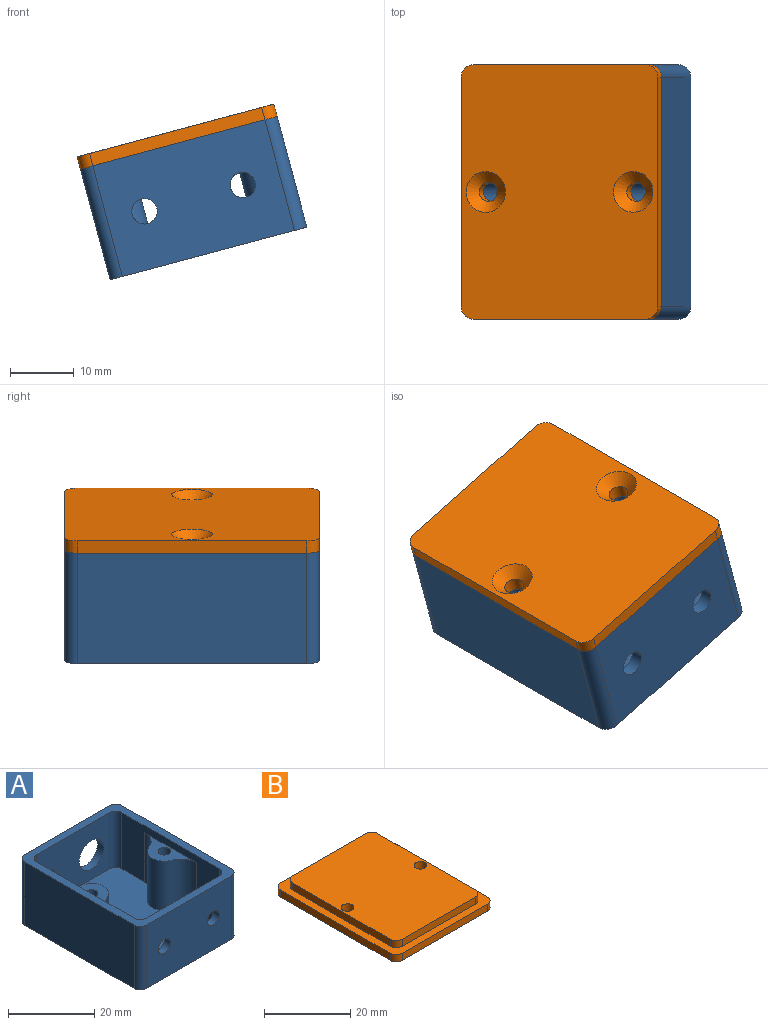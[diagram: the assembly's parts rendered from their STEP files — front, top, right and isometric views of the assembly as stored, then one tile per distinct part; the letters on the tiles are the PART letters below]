
ASSEMBLY  parts=2 mates=1
PART A: 35 faces, bbox 32x40x18 mm
  f0: plane 36x28mm, normal (0,0,1), area 907.9mm2, adj f1,f2,f9,f10,f15,f17,f23,f24
  f1: plane 32x16mm, normal (-1,0,0), area 274.4mm2, adj f0,f7,f18,f23,f24,f27,f30
  f2: plane 32x16mm, normal (1,0,0), area 274.4mm2, adj f0,f7,f16,f25,f26,f28,f29
  f3: plane 28x18mm, normal (0,-1,0), area 478.9mm2, adj f7,f8,f13,f14,f31,f34
  f4: plane 36x18mm, normal (1,0,0), area 648mm2, adj f7,f8,f31,f32
  f5: plane 28x18mm, normal (0,1,0), area 434.1mm2, adj f7,f8,f11,f12,f32,f33
  f6: plane 36x18mm, normal (-1,0,0), area 648mm2, adj f7,f8,f33,f34
  f7: plane 40x32mm, normal (0,0,1), area 272mm2, adj f1,f2,f3,f4,f5,f6,f9,f10
  f8: plane 40x32mm, normal (0,0,-1), area 1276.6mm2, adj f3,f4,f5,f6,f31,f32,f33,f34
  f9: plane 24x16mm, normal (0,-1,0), area 314.1mm2, adj f0,f7,f11,f12,f27,f28
  f10: plane 24x16mm, normal (0,1,0), area 358.9mm2, adj f0,f7,f13,f14,f29,f30
  f11: cylinder r=2.5mm len=5mm, axis (0,1,0), area 31.4mm2, adj f5,f9
  f12: cylinder r=4mm len=8mm, axis (0,1,0), area 50.3mm2, adj f5,f9
  f13: cylinder r=2mm len=4mm, axis (0,-1,0), area 25.1mm2, adj f3,f10
  f14: cylinder r=2mm len=4mm, axis (0,-1,0), area 25.1mm2, adj f3,f10
  f15: cylinder r=4mm len=14mm, axis (0,0,-1), area 137.9mm2, adj f0,f16,f25,f26
  f16: plane 16.97x6mm, normal (0,0,1), area 41.2mm2, adj f2,f15,f21,f25,f26
  f17: cylinder r=4mm len=14mm, axis (0,0,-1), area 137.9mm2, adj f0,f18,f23,f24
  f18: plane 16.97x6mm, normal (0,0,1), area 41.2mm2, adj f1,f17,f19,f23,f24
  f19: cylinder r=1.5mm len=8mm, axis (0,0,1), area 75.4mm2, adj f18,f20
  f20: plane 3x3mm, normal (0,0,1), area 7.1mm2, adj f19
  f21: cylinder r=1.5mm len=8mm, axis (0,0,1), area 75.4mm2, adj f16,f22
  f22: plane 3x3mm, normal (0,0,1), area 7.1mm2, adj f21
  f23: cylinder r=5mm len=14mm, axis (0,0,-1), area 86.2mm2, adj f0,f1,f17,f18
  f24: cylinder r=5mm len=14mm, axis (0,0,-1), area 86.2mm2, adj f0,f1,f17,f18
  f25: cylinder r=5mm len=14mm, axis (0,0,-1), area 86.2mm2, adj f0,f2,f15,f16
  f26: cylinder r=5mm len=14mm, axis (0,0,-1), area 86.2mm2, adj f0,f2,f15,f16
  f27: cylinder r=2mm len=16mm, axis (0,0,-1), area 50.3mm2, adj f0,f1,f7,f9
  f28: cylinder r=2mm len=16mm, axis (0,0,1), area 50.3mm2, adj f0,f2,f7,f9
  f29: cylinder r=2mm len=16mm, axis (0,0,-1), area 50.3mm2, adj f0,f2,f7,f10
  f30: cylinder r=2mm len=16mm, axis (0,0,1), area 50.3mm2, adj f0,f1,f7,f10
  f31: cylinder r=2mm len=18mm, axis (0,0,1), area 56.5mm2, adj f3,f4,f7,f8
  f32: cylinder r=2mm len=18mm, axis (0,0,-1), area 56.5mm2, adj f4,f5,f7,f8
  f33: cylinder r=2mm len=18mm, axis (0,0,1), area 56.5mm2, adj f5,f6,f7,f8
  f34: cylinder r=2mm len=18mm, axis (0,0,-1), area 56.5mm2, adj f3,f6,f7,f8
PART B: 23 faces, bbox 32x40x4 mm
  f0: plane 28x2mm, normal (0,-1,0), area 56mm2, adj f4,f5,f19,f22
  f1: plane 36x2mm, normal (1,0,0), area 72mm2, adj f4,f5,f19,f20
  f2: plane 28x2mm, normal (0,1,0), area 56mm2, adj f4,f5,f20,f21
  f3: plane 36x2mm, normal (-1,0,0), area 72mm2, adj f4,f5,f21,f22
  f4: plane 40x32mm, normal (0,0,1), area 272mm2, adj f0,f1,f2,f3,f6,f7,f8,f9
  f5: plane 40x32mm, normal (0,0,-1), area 1212.2mm2, adj f0,f1,f2,f3,f17,f18,f19,f20
  f6: cylinder r=2mm len=2mm, axis (0,0,-1), area 6.3mm2, adj f4,f7,f13,f14
  f7: plane 24x2mm, normal (0,1,0), area 48mm2, adj f4,f6,f8,f14
  f8: cylinder r=2mm len=2mm, axis (0,0,-1), area 6.3mm2, adj f4,f7,f9,f14
  f9: plane 32x2mm, normal (-1,0,0), area 64mm2, adj f4,f8,f10,f14
  f10: cylinder r=2mm len=2mm, axis (0,0,-1), area 6.3mm2, adj f4,f9,f11,f14
  f11: plane 24x2mm, normal (0,-1,0), area 48mm2, adj f4,f10,f12,f14
  f12: cylinder r=2mm len=2mm, axis (0,0,-1), area 6.3mm2, adj f4,f11,f13,f14
  f13: plane 32x2mm, normal (1,0,0), area 64mm2, adj f4,f6,f12,f14
  f14: plane 36x28mm, normal (0,0,1), area 990.4mm2, adj f6,f7,f8,f9,f10,f11,f12,f13
  f15: cylinder r=1.5mm len=3mm, axis (0,0,-1), area 21.7mm2, adj f14,f18
  f16: cylinder r=1.5mm len=3mm, axis (0,0,-1), area 21.7mm2, adj f14,f17
  f17: cone r=1.5mm half-angle=45deg, axis (0,0,-1), area 35.5mm2, adj f5,f16
  f18: cone r=1.5mm half-angle=45deg, axis (0,0,-1), area 35.5mm2, adj f5,f15
  f19: cylinder r=2mm len=2mm, axis (0,0,1), area 6.3mm2, adj f0,f1,f4,f5
  f20: cylinder r=2mm len=2mm, axis (0,0,-1), area 6.3mm2, adj f1,f2,f4,f5
  f21: cylinder r=2mm len=2mm, axis (0,0,1), area 6.3mm2, adj f2,f3,f4,f5
  f22: cylinder r=2mm len=2mm, axis (0,0,-1), area 6.3mm2, adj f0,f3,f4,f5
PLACE A rot(axis=(0,-1,0),15deg) t=(-11.41,4.62,3.46)mm
PLACE B rot(axis=(0,1,0),165deg) t=(-16.59,4.62,22.78)mm
MATE revolute A.f17 <-> B.f16  axis (-0.26,0,0.97) through (-3.96,4.62,22.02)mm
